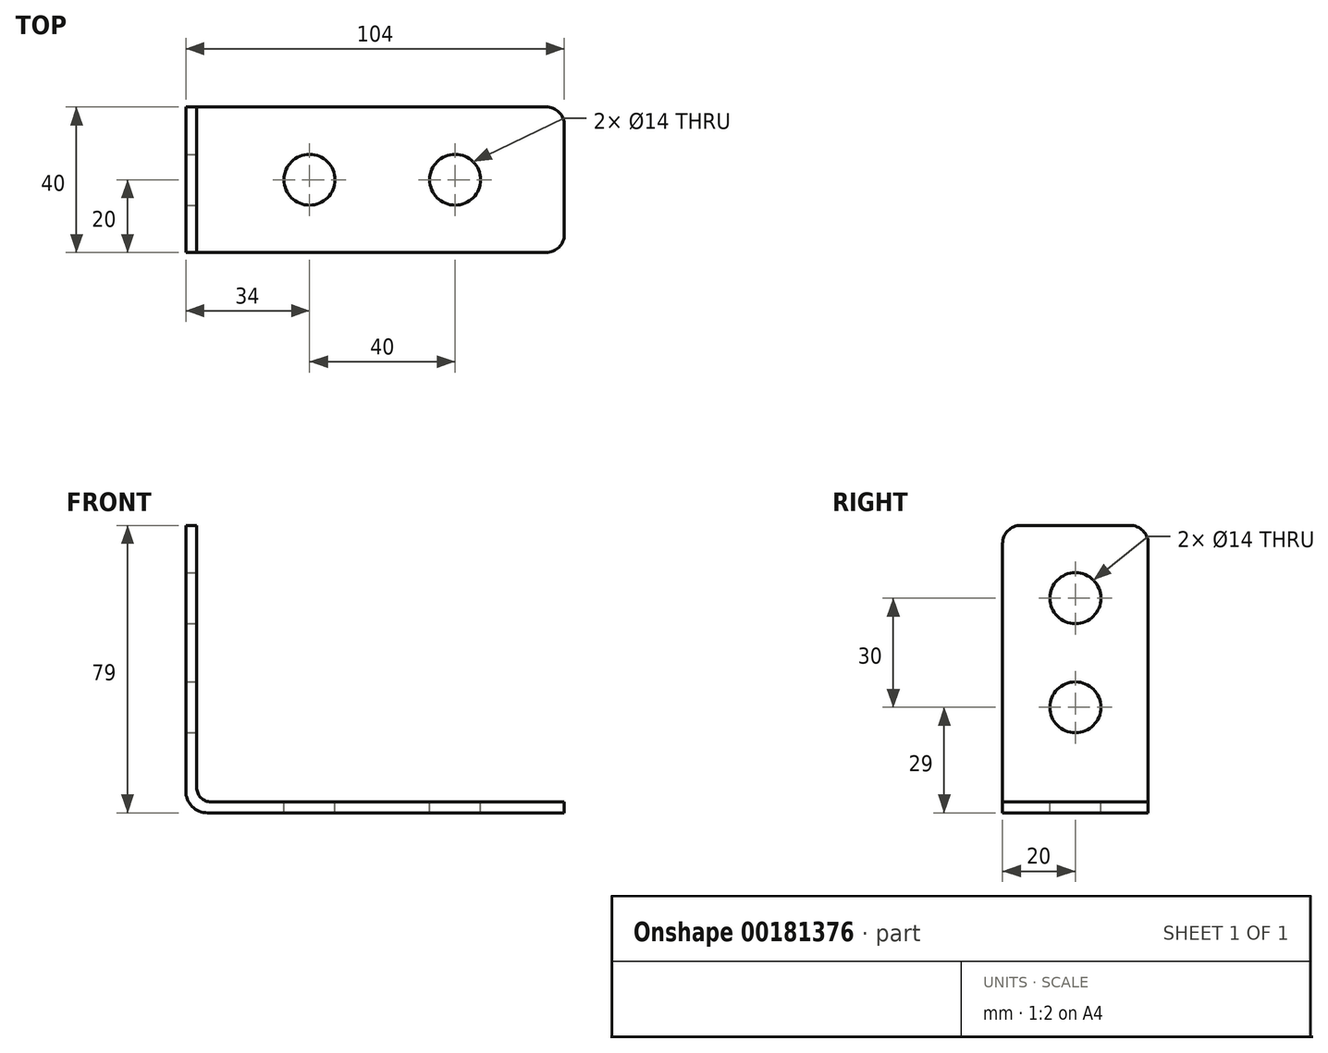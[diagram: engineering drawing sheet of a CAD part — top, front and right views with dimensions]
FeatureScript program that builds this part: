
annotation { "Feature Type Name" : "Feature", "Feature Type Description" : "" }
export const myFeature = defineFeature(function(context is Context, id is Id, definition is map)
    precondition{}
    {
        {
            var Q0;
            Q0=qCreatedBy(makeId("Front.planeOp"),FACE);
            var sketch = newSketch(context, id + "F0", { "sketchPlane" : qUnion([Q0])});
            skLineSegment(sketch, "E0", {"start": v(0, 6) * mm, "end": v(0, 79) * mm});
            skLineSegment(sketch, "E1", {"start": v(0, 79) * mm, "end": v(3, 79) * mm});
            skLineSegment(sketch, "E2", {"start": v(3, 79) * mm, "end": v(3, 7) * mm});
            skLineSegment(sketch, "E3", {"start": v(7, 3) * mm, "end": v(104, 3) * mm});
            skLineSegment(sketch, "E4", {"start": v(104, 3) * mm, "end": v(104, 0) * mm});
            skLineSegment(sketch, "E5", {"start": v(104, 0) * mm, "end": v(6, 0) * mm});
            skPoint(sketch, "E6.visualSharp", {"position": v(3, 3) * mm});
            skArc(sketch, "E6.filletArc", {"start": v(3, 7) * mm, "mid": v(4.17, 4.17) * mm, "end": v(7, 3) * mm});
            skPoint(sketch, "E7.visualSharp", {"position": v(0, 0) * mm});
            skArc(sketch, "E7.filletArc", {"start": v(0, 6) * mm, "mid": v(1.76, 1.76) * mm, "end": v(6, 0) * mm});
            skSolve(sketch);
        }
        {
            var Q0;
            Q0=makeQuery(id+"F0.imprint","IMPRINT",FACE,{"disambiguationData":[TD([[makeQuery(id+"F0.imprint","IMPRINT",EDGE,{"derivedFrom":sQuery(id+"F0.wireOp",EDGE,"E0")}),-1.0]])]});
            extrude(context, id + "F1", {"entities" : qUnion([Q0]), "endBound" : BoundingType.SYMMETRIC, "depth" : 40 * mm});
        }
        {
            var Q0;
            Q0=makeQuery(id+"F1.opExtrude","CAP_EDGE",EDGE,{"disambiguationData":[OSD([sQuery(id+"F0.wireOp",EDGE,"E1")])],"isStart":false});
            var Q1;
            Q1=makeQuery(id+"F1.opExtrude","CAP_EDGE",EDGE,{"disambiguationData":[OSD([sQuery(id+"F0.wireOp",EDGE,"E1")])],"isStart":true});
            var Q2;
            Q2=makeQuery(id+"F1.opExtrude","CAP_EDGE",EDGE,{"disambiguationData":[OSD([sQuery(id+"F0.wireOp",EDGE,"E4")])],"isStart":true});
            var Q3;
            Q3=makeQuery(id+"F1.opExtrude","CAP_EDGE",EDGE,{"disambiguationData":[OSD([sQuery(id+"F0.wireOp",EDGE,"E4")])],"isStart":false});
            fillet(context, id + "F2", {"entities" : qUnion([Q0, Q1, Q2, Q3]), "radius" : 5 * mm, "tangentPropagation" : true, "allowEdgeOverflow" : false});
        }
        {
            var Q0;
            Q0=makeQuery(id+"F1.opExtrude","SWEPT_FACE",FACE,{"disambiguationData":[OSD([sQuery(id+"F0.wireOp",EDGE,"E3")])]});
            var sketch = newSketch(context, id + "F3", { "sketchPlane" : qUnion([Q0])});
            skCircle(sketch, "E8", {"center": v(34, 0) * mm, "radius": 7 * mm});
            skCircle(sketch, "E9", {"center": v(74, 0) * mm, "radius": 7 * mm});
            skSolve(sketch);
        }
        {
            var Q0;
            Q0 = qSketchRegion(id + "F3", true);
            extrude(context, id + "F4", {"entities" : qUnion([Q0]), "operationType" : NewBodyOperationType.REMOVE, "oppositeDirection" : true, "depth" : 25 * mm});
        }
        {
            var Q0;
            Q0=makeQuery(id+"F1.opExtrude","SWEPT_FACE",FACE,{"disambiguationData":[OSD([sQuery(id+"F0.wireOp",EDGE,"E2")])]});
            var sketch = newSketch(context, id + "F5", { "sketchPlane" : qUnion([Q0])});
            skCircle(sketch, "E10", {"center": v(0, 59) * mm, "radius": 7 * mm});
            skCircle(sketch, "E11", {"center": v(0, 29) * mm, "radius": 7 * mm});
            skSolve(sketch);
        }
        {
            var Q0;
            Q0 = qSketchRegion(id + "F5", true);
            extrude(context, id + "F6", {"entities" : qUnion([Q0]), "operationType" : NewBodyOperationType.REMOVE, "oppositeDirection" : true, "depth" : 25 * mm});
        }
    });
